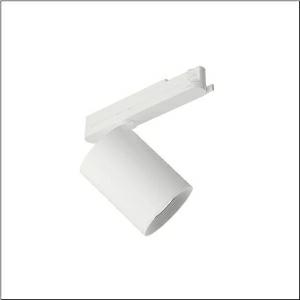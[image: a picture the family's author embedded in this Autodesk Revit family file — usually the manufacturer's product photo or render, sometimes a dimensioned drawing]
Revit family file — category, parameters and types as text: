
# Revit family: spot_21_51se12mbb5b
name_source: partatom
category: Lighting Fixtures
units: mm (PartAtom-declared; Revit-internal decimal feet)

## family parameters
Cut with Voids When Loaded = No
Host = Face
Light Source = No
Part Type = Normal
Room Calculation Point = No
Round Connector Dimension = Use Diameter
Shared = No

## types (1)
- --- (1 x LED, 5300 lm, 41.7 W, 3000K)
    Apparent Load = 42 VA
    CIE Flux Codes = 95 98 99 100 100
    Color Rendering = 90
    Color Temperature = 3000K
    Default Elevation = 1800 mm
    Description = Spot 21, directional spotlight, light control with lens, of PMMA, LED rated luminous flux: 5.100lm, light colour: 930, control gear: ECG Multilumen, with 3-phase adapter, mains connection: 220..240V, AC, 50/60Hz, of aluminium, traffic white (RAL 9016), length: 213mm, diameter: 105mm, protection rating (complete): IP20, insulation class (complete): insulation class I (protective earthing), certification: CE, impact resistance: IK02, permissible ambient temperature for indoor applications: -20..+40°C, packaging unit: 1 piece
    Height = 175 mm
    Lamp = 1 x LED
    Lamp Light Flux = 5300 lm
    Lamp Power = 41.7 W
    Lamp count = 1
    Length = 105 mm
    Luminous efficacy = 127 lm/W
    Manufacturer = Siteco
    ModVariant = No
    Model = 51SE12MBB5B
    Mounting Place = Ceiling
    Mounting Type = Pendant
    Number of Poles = 1
    OnlyDefault = Yes
    Power Factor = 1
    Product Name = Spot 21
    Product group = directional spotlight
    ProductGroupID = 905
    Protection Class = Protection class I
    Protection Degree = IP 20
    RLX_Detail_Level = 1
    RLX_Emergency_Light_Flux = 0 lm
    RLX_Emergency_Type = 0
    RLX_Emergency_Type_DB = No
    RlxData = <blob elided: 17629 chars, md5=dbdc0b13>
    Socket = socket
    Standby Power = 0 W
    System Light Flux = 5300 lm
    System Power = 42 W
    Type Comments = factory setting: luminous flux: 100 % | (ON | ON | ON | ON) | 1050 mA
    Type Image = l_1003976.jpg
    URL = http://relux.com
    VarID = @adj_165793
    Voltage = 0 V
    Weight = 0.00 kg
    Width = 0 mm  [stored 0 ft]

note: [stored X ft] marks values corroborated as IEEE doubles in the binary element streams (Revit-internal decimal feet)

## geometry (parser evidence)
native form markers: Blend x4, Sweep x9
no freeform markers — native parametric forms only
